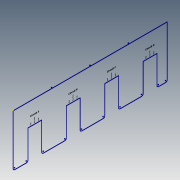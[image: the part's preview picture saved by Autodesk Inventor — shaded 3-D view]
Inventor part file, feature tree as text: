
AUTODESK INVENTOR PART (.ipt)
format: ipt  version: 2020.5 (Build 245400000, 400)  size: 169,472 bytes
history: native  units: mm
features: sketch x1
ambient origin geometry x8: Origin, YZ Plane, XZ Plane, XY Plane, X Axis, Y Axis, Z Axis, Center Point
feature tree (1):
  sketch  "Sketch31"  dims[d13=18.0mm d14=60.0mm d692=11.8mm d693=2.1mm d694=7.08mm d695=1.33mm d696=3.18mm d697=1.05mm d698=1.05mm d699=3.3mm d700=11.8mm d701=2.1mm d702=7.08mm d703=1.33mm d704=3.18mm d705=1.05mm d706=1.05mm d707=3.3mm d708=17.6mm d709=27.899893mm d710=25.82mm d711=21.92mm d712=25.7mm d713=27.604893mm d714=22.664893mm d715=17.444893mm d716=22.100107mm d717=17.6mm d718=22.395107mm d719=25.82mm d720=21.92mm d721=27.335107mm d722=25.7mm d723=32.555107mm d724=11.8mm d725=2.1mm d726=7.08mm d727=1.33mm d728=3.18mm d729=1.05mm d730=1.05mm d731=3.3mm d732=11.9mm d733=2.1mm d734=7.08mm d735=1.33mm d736=3.18mm d737=1.05mm d738=1.05mm d739=3.3mm d740=17.6mm d741=27.899893mm d742=25.82mm d743=21.92mm d744=25.7mm d745=27.604893mm d746=22.664893mm d747=17.444893mm d748=22.100107mm d749=17.6mm d750=22.395107mm d751=25.82mm d752=21.92mm d753=27.335107mm d754=25.7mm d755=32.555107mm]
